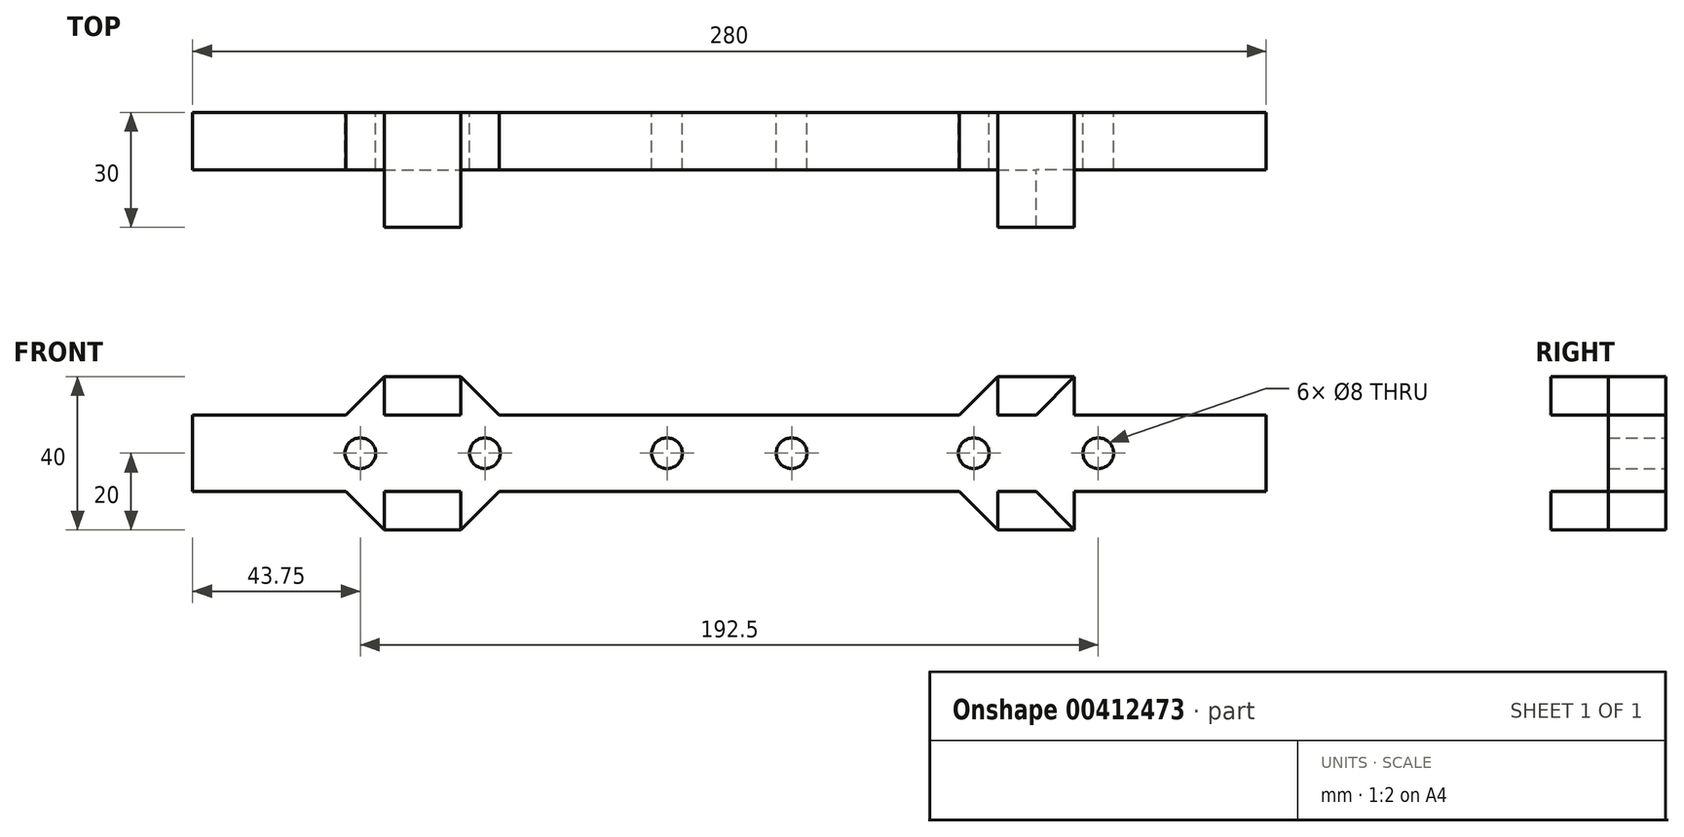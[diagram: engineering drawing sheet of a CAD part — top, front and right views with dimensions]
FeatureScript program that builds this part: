
annotation { "Feature Type Name" : "Feature", "Feature Type Description" : "" }
export const myFeature = defineFeature(function(context is Context, id is Id, definition is map)
    precondition{}
    {
        {
            var Q0;
            Q0=qCreatedBy(makeId("Front.planeOp"),FACE);
            var sketch = newSketch(context, id + "F0", { "sketchPlane" : qUnion([Q0])});
            skPoint(sketch, "E0", {"position": v(-140, 0) * mm});
            skLineSegment(sketch, "E1.bottom", {"start": v(-140, 0) * mm, "end": v(140, 0) * mm});
            skLineSegment(sketch, "E1.top", {"start": v(-140, 20) * mm, "end": v(140, 20) * mm});
            skLineSegment(sketch, "E1.left", {"start": v(-140, 0) * mm, "end": v(-140, 20) * mm});
            skLineSegment(sketch, "E1.right", {"start": v(140, 0) * mm, "end": v(140, 20) * mm});
            skLineSegment(sketch, "E2.bottom", {"start": v(-90, 30) * mm, "end": v(-70, 30) * mm});
            skLineSegment(sketch, "E2.top", {"start": v(-90, -10) * mm, "end": v(-70, -10) * mm});
            skLineSegment(sketch, "E2.left", {"start": v(-90, 30) * mm, "end": v(-90, -10) * mm});
            skLineSegment(sketch, "E2.right", {"start": v(-70, 30) * mm, "end": v(-70, -10) * mm});
            skLineSegment(sketch, "E3.bottom", {"start": v(70, 30) * mm, "end": v(90, 30) * mm});
            skLineSegment(sketch, "E3.top", {"start": v(70, -10) * mm, "end": v(90, -10) * mm});
            skLineSegment(sketch, "E3.left", {"start": v(70, 30) * mm, "end": v(70, -10) * mm});
            skLineSegment(sketch, "E3.right", {"start": v(90, 30) * mm, "end": v(90, -10) * mm});
            skCircle(sketch, "E4", {"center": v(-63.75, 10) * mm, "radius": 4 * mm});
            skCircle(sketch, "E5", {"center": v(63.75, 10) * mm, "radius": 4 * mm});
            skCircle(sketch, "E6", {"center": v(-96.25, 10) * mm, "radius": 4 * mm});
            skCircle(sketch, "E7", {"center": v(96.25, 10) * mm, "radius": 4 * mm});
            skCircle(sketch, "E8", {"center": v(-16.25, 10) * mm, "radius": 4 * mm});
            skCircle(sketch, "E9", {"center": v(16.25, 10) * mm, "radius": 4 * mm});
            skSolve(sketch);
        }
        {
            var Q0;
            {var subQ5=sQuery(id+"F0.wireOp",EDGE,"E1.left");Q0=makeQuery(id+"F0.imprint","IMPRINT",FACE,{"disambiguationData":[TD([[makeQuery(id+"F0.imprint","IMPRINT",EDGE,{"derivedFrom":subQ5}),-1.0]])]});}
            var Q1;
            {var subQ0=sQuery(id+"F0.wireOp",EDGE,"E2.left");var subQ1=sQuery(id+"F0.wireOp",EDGE,"E1.bottom");var subQ2=makeQuery(id+"F0.imprint","INTERSECT",VERTEX,{"derivedFrom":[subQ1,subQ0]});Q1=makeQuery(id+"F0.imprint","IMPRINT",FACE,{"disambiguationData":[TD([[makeQuery(id+"F0.imprint","IMPRINT",EDGE,{"disambiguationData":[TD([[subQ2,-1.0]])],"derivedFrom":subQ1}),1.0]])]});}
            var Q2;
            Q2=makeQuery(id+"F0.imprint","IMPRINT",FACE,{"disambiguationData":[TD([[makeQuery(id+"F0.imprint","IMPRINT",EDGE,{"derivedFrom":sQuery(id+"F0.wireOp",EDGE,"690dFIF3-Smrc-JWHr-bkvG-Utc56nn6OeRY")}),-1.0]])]});
            var Q3;
            {var subQ0=sQuery(id+"F0.wireOp",EDGE,"E3.left");var subQ1=sQuery(id+"F0.wireOp",EDGE,"E1.bottom");var subQ2=makeQuery(id+"F0.imprint","INTERSECT",VERTEX,{"derivedFrom":[subQ1,subQ0]});Q3=makeQuery(id+"F0.imprint","IMPRINT",FACE,{"disambiguationData":[TD([[makeQuery(id+"F0.imprint","IMPRINT",EDGE,{"disambiguationData":[TD([[subQ2,-1.0]])],"derivedFrom":subQ1}),1.0]])]});}
            var Q4;
            {var subQ5=sQuery(id+"F0.wireOp",EDGE,"E1.right");Q4=makeQuery(id+"F0.imprint","IMPRINT",FACE,{"disambiguationData":[TD([[makeQuery(id+"F0.imprint","IMPRINT",EDGE,{"derivedFrom":subQ5}),1.0]])]});}
            var Q5;
            Q5=makeQuery(id+"F0.imprint","IMPRINT",FACE,{"disambiguationData":[TD([[makeQuery(id+"F0.imprint","IMPRINT",EDGE,{"derivedFrom":sQuery(id+"F0.wireOp",EDGE,"E4")}),-1.0]])]});
            extrude(context, id + "F1", {"entities" : qUnion([Q0, Q1, Q2, Q3, Q4, Q5]), "depth" : 15 * mm});
        }
        {
            var Q0;
            {var subQ5=sQuery(id+"F0.wireOp",EDGE,"E3.bottom");Q0=makeQuery(id+"F0.imprint","IMPRINT",FACE,{"disambiguationData":[TD([[makeQuery(id+"F0.imprint","IMPRINT",EDGE,{"derivedFrom":subQ5}),-1.0]])]});}
            var Q1;
            {var subQ5=sQuery(id+"F0.wireOp",EDGE,"E2.bottom");Q1=makeQuery(id+"F0.imprint","IMPRINT",FACE,{"disambiguationData":[TD([[makeQuery(id+"F0.imprint","IMPRINT",EDGE,{"derivedFrom":subQ5}),-1.0]])]});}
            var Q2;
            {var subQ5=sQuery(id+"F0.wireOp",EDGE,"E2.top");Q2=makeQuery(id+"F0.imprint","IMPRINT",FACE,{"disambiguationData":[TD([[makeQuery(id+"F0.imprint","IMPRINT",EDGE,{"derivedFrom":subQ5}),1.0]])]});}
            var Q3;
            {var subQ5=sQuery(id+"F0.wireOp",EDGE,"E3.top");Q3=makeQuery(id+"F0.imprint","IMPRINT",FACE,{"disambiguationData":[TD([[makeQuery(id+"F0.imprint","IMPRINT",EDGE,{"derivedFrom":subQ5}),1.0]])]});}
            extrude(context, id + "F2", {"entities" : qUnion([Q0, Q1, Q2, Q3]), "operationType" : NewBodyOperationType.ADD, "depth" : 30 * mm});
        }
        {
            var Q0;
            {var subQ0=sQuery(id+"F0.wireOp",EDGE,"E1.top");var subQ1=sQuery(id+"F0.wireOp",EDGE,"E3.left");Q0=makeQuery(id+"F2.boolean.opBoolean","SPLIT",EDGE,{"disambiguationData":[topologyDisambiguationEdgeConnected([makeQuery(id+"F1.opExtrude","SWEPT_FACE",FACE,{"disambiguationData":[OSD([subQ0])]})])],"derivedFrom":makeQuery(id+"F2.opExtrude","SWEPT_EDGE",EDGE,{"disambiguationData":[OSD([subQ0,subQ1])]})});}
            var Q1;
            {var subQ0=sQuery(id+"F0.wireOp",EDGE,"E1.top");var subQ1=sQuery(id+"F0.wireOp",EDGE,"E3.right");Q1=makeQuery(id+"F2.boolean.opBoolean","SPLIT",EDGE,{"disambiguationData":[topologyDisambiguationEdgeConnected([makeQuery(id+"F1.opExtrude","SWEPT_FACE",FACE,{"disambiguationData":[OSD([subQ0])]})])],"derivedFrom":makeQuery(id+"F2.opExtrude","SWEPT_EDGE",EDGE,{"disambiguationData":[OSD([subQ0,subQ1])]})});}
            var Q2;
            {var subQ0=sQuery(id+"F0.wireOp",EDGE,"E1.top");var subQ1=sQuery(id+"F0.wireOp",EDGE,"E2.right");Q2=makeQuery(id+"F2.boolean.opBoolean","SPLIT",EDGE,{"disambiguationData":[topologyDisambiguationEdgeConnected([makeQuery(id+"F1.opExtrude","SWEPT_FACE",FACE,{"disambiguationData":[OSD([subQ0])]})])],"derivedFrom":makeQuery(id+"F2.opExtrude","SWEPT_EDGE",EDGE,{"disambiguationData":[OSD([subQ0,subQ1])]})});}
            var Q3;
            {var subQ0=sQuery(id+"F0.wireOp",EDGE,"E1.top");var subQ1=sQuery(id+"F0.wireOp",EDGE,"E2.left");Q3=makeQuery(id+"F2.boolean.opBoolean","SPLIT",EDGE,{"disambiguationData":[topologyDisambiguationEdgeConnected([makeQuery(id+"F1.opExtrude","SWEPT_FACE",FACE,{"disambiguationData":[OSD([subQ0])]})])],"derivedFrom":makeQuery(id+"F2.opExtrude","SWEPT_EDGE",EDGE,{"disambiguationData":[OSD([subQ0,subQ1])]})});}
            var Q4;
            {var subQ0=sQuery(id+"F0.wireOp",EDGE,"E1.bottom");var subQ1=sQuery(id+"F0.wireOp",EDGE,"E2.left");Q4=makeQuery(id+"F2.boolean.opBoolean","SPLIT",EDGE,{"disambiguationData":[topologyDisambiguationEdgeConnected([makeQuery(id+"F1.opExtrude","SWEPT_FACE",FACE,{"disambiguationData":[OSD([subQ0])]})])],"derivedFrom":makeQuery(id+"F2.opExtrude","SWEPT_EDGE",EDGE,{"disambiguationData":[OSD([subQ0,subQ1])]})});}
            var Q5;
            {var subQ0=sQuery(id+"F0.wireOp",EDGE,"E1.bottom");var subQ1=sQuery(id+"F0.wireOp",EDGE,"E2.right");Q5=makeQuery(id+"F2.boolean.opBoolean","SPLIT",EDGE,{"disambiguationData":[topologyDisambiguationEdgeConnected([makeQuery(id+"F1.opExtrude","SWEPT_FACE",FACE,{"disambiguationData":[OSD([subQ0])]})])],"derivedFrom":makeQuery(id+"F2.opExtrude","SWEPT_EDGE",EDGE,{"disambiguationData":[OSD([subQ0,subQ1])]})});}
            var Q6;
            {var subQ0=sQuery(id+"F0.wireOp",EDGE,"E1.bottom");var subQ1=sQuery(id+"F0.wireOp",EDGE,"E3.left");Q6=makeQuery(id+"F2.boolean.opBoolean","SPLIT",EDGE,{"disambiguationData":[topologyDisambiguationEdgeConnected([makeQuery(id+"F1.opExtrude","SWEPT_FACE",FACE,{"disambiguationData":[OSD([subQ0])]})])],"derivedFrom":makeQuery(id+"F2.opExtrude","SWEPT_EDGE",EDGE,{"disambiguationData":[OSD([subQ0,subQ1])]})});}
            var Q7;
            {var subQ0=sQuery(id+"F0.wireOp",EDGE,"E1.bottom");var subQ1=sQuery(id+"F0.wireOp",EDGE,"E3.right");Q7=makeQuery(id+"F2.boolean.opBoolean","SPLIT",EDGE,{"disambiguationData":[topologyDisambiguationEdgeConnected([makeQuery(id+"F1.opExtrude","SWEPT_FACE",FACE,{"disambiguationData":[OSD([subQ0])]})])],"derivedFrom":makeQuery(id+"F2.opExtrude","SWEPT_EDGE",EDGE,{"disambiguationData":[OSD([subQ0,subQ1])]})});}
            chamfer(context, id + "F3", {"entities" : qUnion([Q0, Q1, Q2, Q3, Q4, Q5, Q6, Q7]), "width" : 10 * mm, "tangentPropagation" : true});
        }
    });
